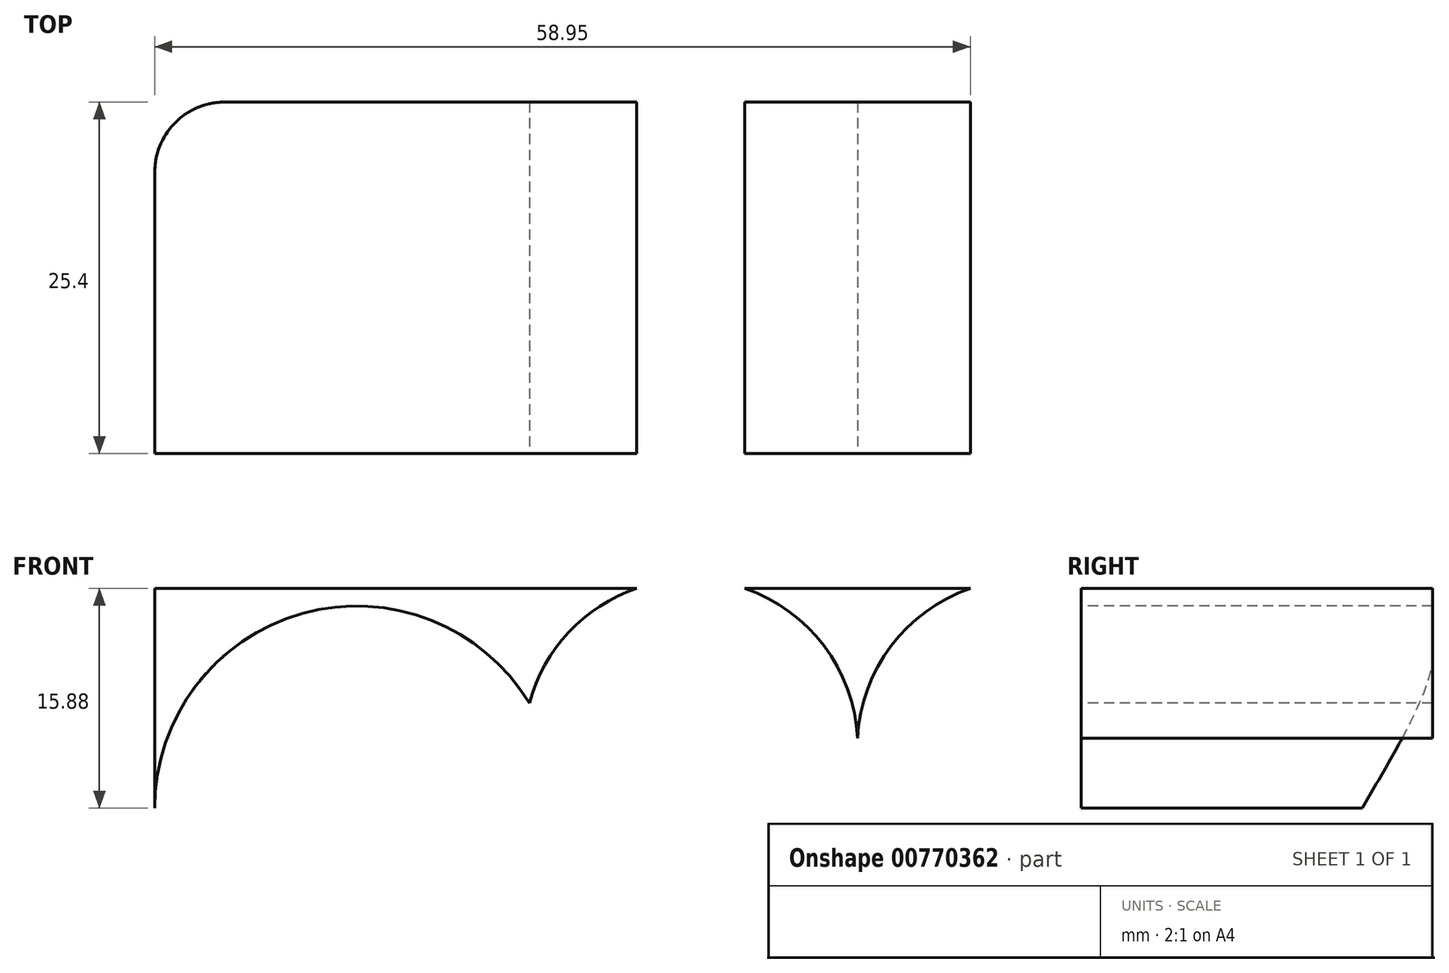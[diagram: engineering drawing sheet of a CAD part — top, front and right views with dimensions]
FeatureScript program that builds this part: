
annotation { "Feature Type Name" : "Feature", "Feature Type Description" : "" }
export const myFeature = defineFeature(function(context is Context, id is Id, definition is map)
    precondition{}
    {
        {
            var Q0;
            Q0=qCreatedBy(makeId("Front.planeOp"),FACE);
            var sketch = newSketch(context, id + "F0", { "sketchPlane" : qUnion([Q0])});
            skLineSegment(sketch, "E0.bottom", {"start": v(50.8, -25.4) * mm, "end": v(-50.8, -25.4) * mm});
            skLineSegment(sketch, "E0.top", {"start": v(50.8, 25.4) * mm, "end": v(-50.8, 25.4) * mm});
            skLineSegment(sketch, "E0.left", {"start": v(50.8, -25.4) * mm, "end": v(50.8, 25.4) * mm});
            skLineSegment(sketch, "E0.right", {"start": v(-50.8, -25.4) * mm, "end": v(-50.8, 25.4) * mm});
            skPoint(sketch, "E0.middle", {"position": v(0, 0) * mm});
            skEllipse(sketch, "E1", {"center": v(0, -10.41) * mm, "majorRadius": 47.63 * mm, "minorRadius": 9.53 * mm, "majorAxis": v(1, 0)});
            skCircle(sketch, "E2", {"center": v(-36.2, 9.53) * mm, "radius": 8.9 * mm});
            skCircle(sketch, "E3", {"center": v(-12.07, 13.97) * mm, "radius": 8.9 * mm});
            skCircle(sketch, "E4.MirrorC", {"center": v(12.07, 13.97) * mm, "radius": 8.9 * mm});
            skCircle(sketch, "E5.MirrorC", {"center": v(36.2, 9.53) * mm, "radius": 8.9 * mm});
            skSolve(sketch);
        }
        {
            var Q0;
            Q0 = qSketchRegion(id + "F0", true);
            extrude(context, id + "F1", {"entities" : qUnion([Q0]), "depth" : 25.4 * mm, "offsetDistance" : 25.4 * mm});
        }
        {
            var Q0;
            Q0=makeQuery(id+"F1.opExtrude","SWEPT_EDGE",EDGE,{"disambiguationData":[OSD([sQuery(id+"F0.wireOp",EDGE,"E0.bottom"),sQuery(id+"F0.wireOp",EDGE,"E0.left")])]});
            var Q1;
            Q1=makeQuery(id+"F1.opExtrude","SWEPT_EDGE",EDGE,{"disambiguationData":[OSD([sQuery(id+"F0.wireOp",EDGE,"E0.bottom"),sQuery(id+"F0.wireOp",EDGE,"E0.right")])]});
            fillet(context, id + "F2", {"entities" : qUnion([Q0, Q1]), "radius" : 19.05 * mm, "tangentPropagation" : true, "allowEdgeOverflow" : false});
        }
        {
            var Q0;
            Q0=makeQuery(id+"F1.opExtrude","CAP_FACE",FACE,{"disambiguationData":[OSD([sQuery(id+"F0.wireOp",EDGE,"E0.bottom"),sQuery(id+"F0.wireOp",EDGE,"E0.top"),sQuery(id+"F0.wireOp",EDGE,"E0.left"),sQuery(id+"F0.wireOp",EDGE,"E0.right"),sQuery(id+"F0.wireOp",EDGE,"E1"),sQuery(id+"F0.wireOp",EDGE,"E2"),sQuery(id+"F0.wireOp",EDGE,"E3"),sQuery(id+"F0.wireOp",EDGE,"E4.MirrorC"),sQuery(id+"F0.wireOp",EDGE,"E5.MirrorC")])],"isStart":false});
            var sketch = newSketch(context, id + "F3", { "sketchPlane" : qUnion([Q0])});
            skArc(sketch, "E6", {"start": v(0, 14.58) * mm, "mid": v(-12.25, 26.05) * mm, "end": v(-24.14, 14.2) * mm});
            skArc(sketch, "E7", {"start": v(0, 14.58) * mm, "mid": v(12.07, 26.05) * mm, "end": v(24.13, 14.58) * mm});
            skArc(sketch, "E8", {"start": v(50.8, 9.53) * mm, "mid": v(40.14, 23.59) * mm, "end": v(23.73, 17.13) * mm});
            skArc(sketch, "E9", {"start": v(-50.8, 9.52) * mm, "mid": v(-40.14, 23.59) * mm, "end": v(-23.73, 17.13) * mm});
            skSolve(sketch);
        }
        {
            var Q0;
            Q0 = qSketchRegion(id + "F3", true);
            var Q1;
            {var subQ0=sQuery(id+"F3.wireOp",EDGE,"E9");Q1=makeQuery(id+"F3.imprint","IMPRINT",FACE,{"disambiguationData":[TD([[makeQuery(id+"F3.imprint","IMPRINT",EDGE,{"derivedFrom":subQ0}),1.0]])]});}
            var Q2;
            {var subQ0=sQuery(id+"F3.wireOp",EDGE,"E8");Q2=makeQuery(id+"F3.imprint","IMPRINT",FACE,{"disambiguationData":[TD([[makeQuery(id+"F3.imprint","IMPRINT",EDGE,{"derivedFrom":subQ0}),-1.0]])]});}
            extrude(context, id + "F4", {"entities" : qUnion([Q0, Q1, Q2]), "operationType" : NewBodyOperationType.REMOVE, "oppositeDirection" : true, "depth" : 25.4 * mm, "offsetDistance" : 25.4 * mm});
        }
        {
            var Q0;
            Q0=makeQuery(id+"F1.opExtrude","CAP_EDGE",EDGE,{"disambiguationData":[OSD([sQuery(id+"F0.wireOp",EDGE,"E5.MirrorC")])],"isStart":false});
            var Q1;
            Q1=makeQuery(id+"F1.opExtrude","CAP_EDGE",EDGE,{"disambiguationData":[OSD([sQuery(id+"F0.wireOp",EDGE,"E4.MirrorC")])],"isStart":false});
            var Q2;
            Q2=makeQuery(id+"F1.opExtrude","CAP_EDGE",EDGE,{"disambiguationData":[OSD([sQuery(id+"F0.wireOp",EDGE,"E3")])],"isStart":false});
            var Q3;
            Q3=makeQuery(id+"F1.opExtrude","CAP_EDGE",EDGE,{"disambiguationData":[OSD([sQuery(id+"F0.wireOp",EDGE,"E2")])],"isStart":false});
            var Q4;
            Q4=makeQuery(id+"F1.opExtrude","CAP_EDGE",EDGE,{"disambiguationData":[OSD([sQuery(id+"F0.wireOp",EDGE,"E1")])],"isStart":false});
            var Q5;
            Q5=makeQuery(id+"F1.opExtrude","CAP_EDGE",EDGE,{"disambiguationData":[OSD([sQuery(id+"F0.wireOp",EDGE,"E1")])],"isStart":true});
            var Q6;
            Q6=makeQuery(id+"F1.opExtrude","CAP_EDGE",EDGE,{"disambiguationData":[OSD([sQuery(id+"F0.wireOp",EDGE,"E5.MirrorC")])],"isStart":true});
            var Q7;
            Q7=makeQuery(id+"F1.opExtrude","CAP_EDGE",EDGE,{"disambiguationData":[OSD([sQuery(id+"F0.wireOp",EDGE,"E4.MirrorC")])],"isStart":true});
            var Q8;
            Q8=makeQuery(id+"F1.opExtrude","CAP_EDGE",EDGE,{"disambiguationData":[OSD([sQuery(id+"F0.wireOp",EDGE,"E3")])],"isStart":true});
            var Q9;
            Q9=makeQuery(id+"F1.opExtrude","CAP_EDGE",EDGE,{"disambiguationData":[OSD([sQuery(id+"F0.wireOp",EDGE,"E2")])],"isStart":true});
            var Q10;
            Q10=makeQuery(id+"F1.opExtrude","CAP_EDGE",EDGE,{"disambiguationData":[OSD([sQuery(id+"F0.wireOp",EDGE,"E0.left")])],"isStart":true});
            var Q11;
            Q11=makeQuery(id+"F1.opExtrude","CAP_EDGE",EDGE,{"disambiguationData":[OSD([sQuery(id+"F0.wireOp",EDGE,"E0.right")])],"isStart":true});
            fillet(context, id + "F5", {"entities" : qUnion([Q0, Q1, Q2, Q3, Q4, Q5, Q6, Q7, Q8, Q9, Q10, Q11]), "radius" : 5.08 * mm, "tangentPropagation" : true, "allowEdgeOverflow" : false});
        }
    });
